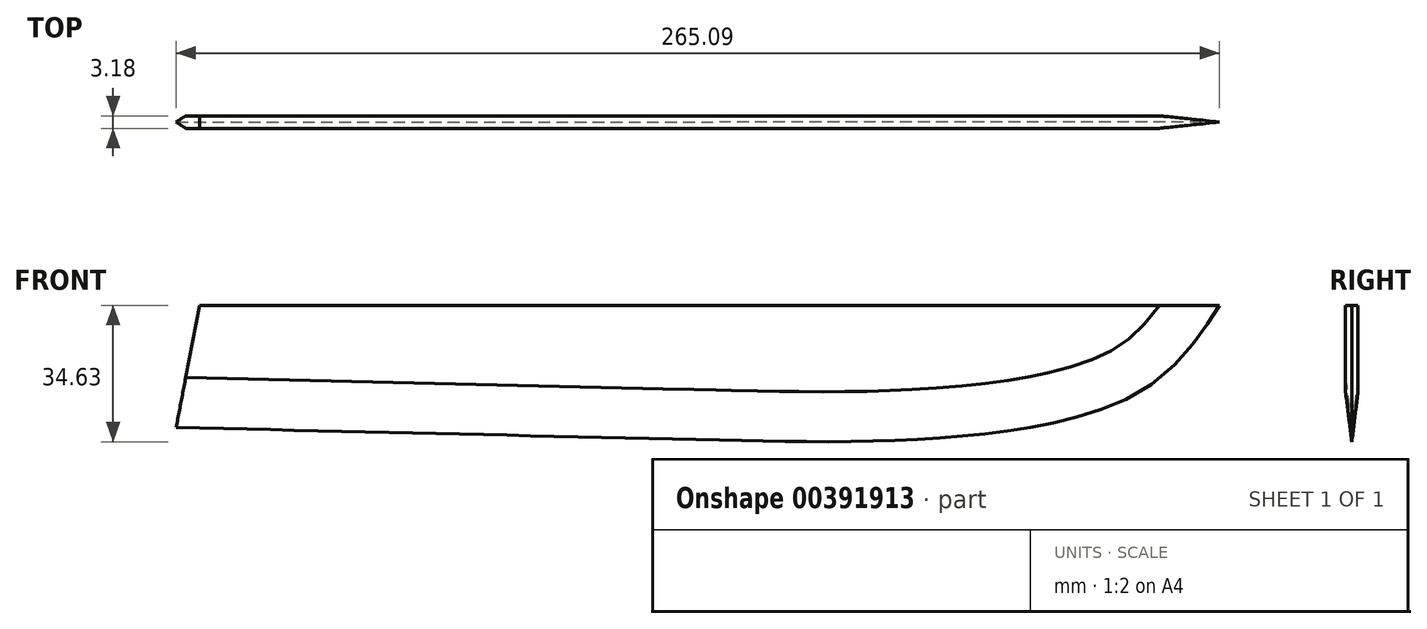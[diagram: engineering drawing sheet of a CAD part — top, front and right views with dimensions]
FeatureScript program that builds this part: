
annotation { "Feature Type Name" : "Feature", "Feature Type Description" : "" }
export const myFeature = defineFeature(function(context is Context, id is Id, definition is map)
    precondition{}
    {
        {
            var Q0;
            Q0=qCreatedBy(makeId("Front.planeOp"),FACE);
            var sketch = newSketch(context, id + "F0", { "sketchPlane" : qUnion([Q0])});
            skLineSegment(sketch, "E0", {"start": v(150.55, 0) * mm, "end": v(23.55, 0) * mm});
            skFitSpline(sketch, "E1", {"points": [v(150.55, 0) * mm, v(130.31, -21.95) * mm, v(77.9, -33.76) * mm, v(23.55, -34.23) * mm], "startDerivative": vector(-58.97, -90.4) * mm, "endDerivative": vector(-144.5, 3.37) * mm});
            skLineSegment(sketch, "E2", {"start": v(23.55, 0) * mm, "end": v(-108.6, 0) * mm});
            skFitSpline(sketch, "E3", {"points": [v(23.55, -34.23) * mm, v(15.55, -24.23) * mm, v(4.58, -20.27) * mm, v(-11.88, -20.27) * mm, v(-47.23, -24.54) * mm, v(-79.85, -27.89) * mm, v(-111.9, -17.23) * mm], "startDerivative": vector(-57.04, 90.54) * mm, "endDerivative": vector(-157.66, 70.4) * mm});
            skLineSegment(sketch, "E4", {"start": v(-108.6, 0) * mm, "end": v(-111.9, -17.23) * mm});
            skSolve(sketch);
        }
        {
            var Q0;
            Q0=makeQuery(id+"F0.imprint","IMPRINT",FACE,{"disambiguationData":[TD([[makeQuery(id+"F0.imprint","IMPRINT",EDGE,{"derivedFrom":sQuery(id+"F0.wireOp",EDGE,"E0")}),1.0]])]});
            var Q1;
            Q1=makeQuery(id+"F0.imprint","IMPRINT",FACE,{"disambiguationData":[TD([[makeQuery(id+"F0.imprint","IMPRINT",EDGE,{"derivedFrom":sQuery(id+"F0.wireOp",EDGE,"d68a86fd-f0f5-4db8-8e23-d1abf0c0f7d5")}),-1.0]])]});
            extrude(context, id + "F1", {"entities" : qUnion([Q0, Q1]), "depth" : 3.17 * mm});
        }
        {
            var Q0;
            Q0=makeQuery(id+"F1.opExtrude","CAP_EDGE",EDGE,{"disambiguationData":[OSD([sQuery(id+"F0.wireOp",EDGE,"E1")])],"isStart":true});
            var Q1;
            Q1=makeQuery(id+"F1.opExtrude","CAP_EDGE",EDGE,{"disambiguationData":[OSD([sQuery(id+"F0.wireOp",EDGE,"E1")])],"isStart":false});
            chamfer(context, id + "F2", {"entities" : qUnion([Q0, Q1]), "chamferType" : ChamferType.TWO_OFFSETS, "width1" : 12.7 * mm, "oppositeDirection" : false, "width2" : 1.59 * mm, "tangentPropagation" : true});
        }
    });
